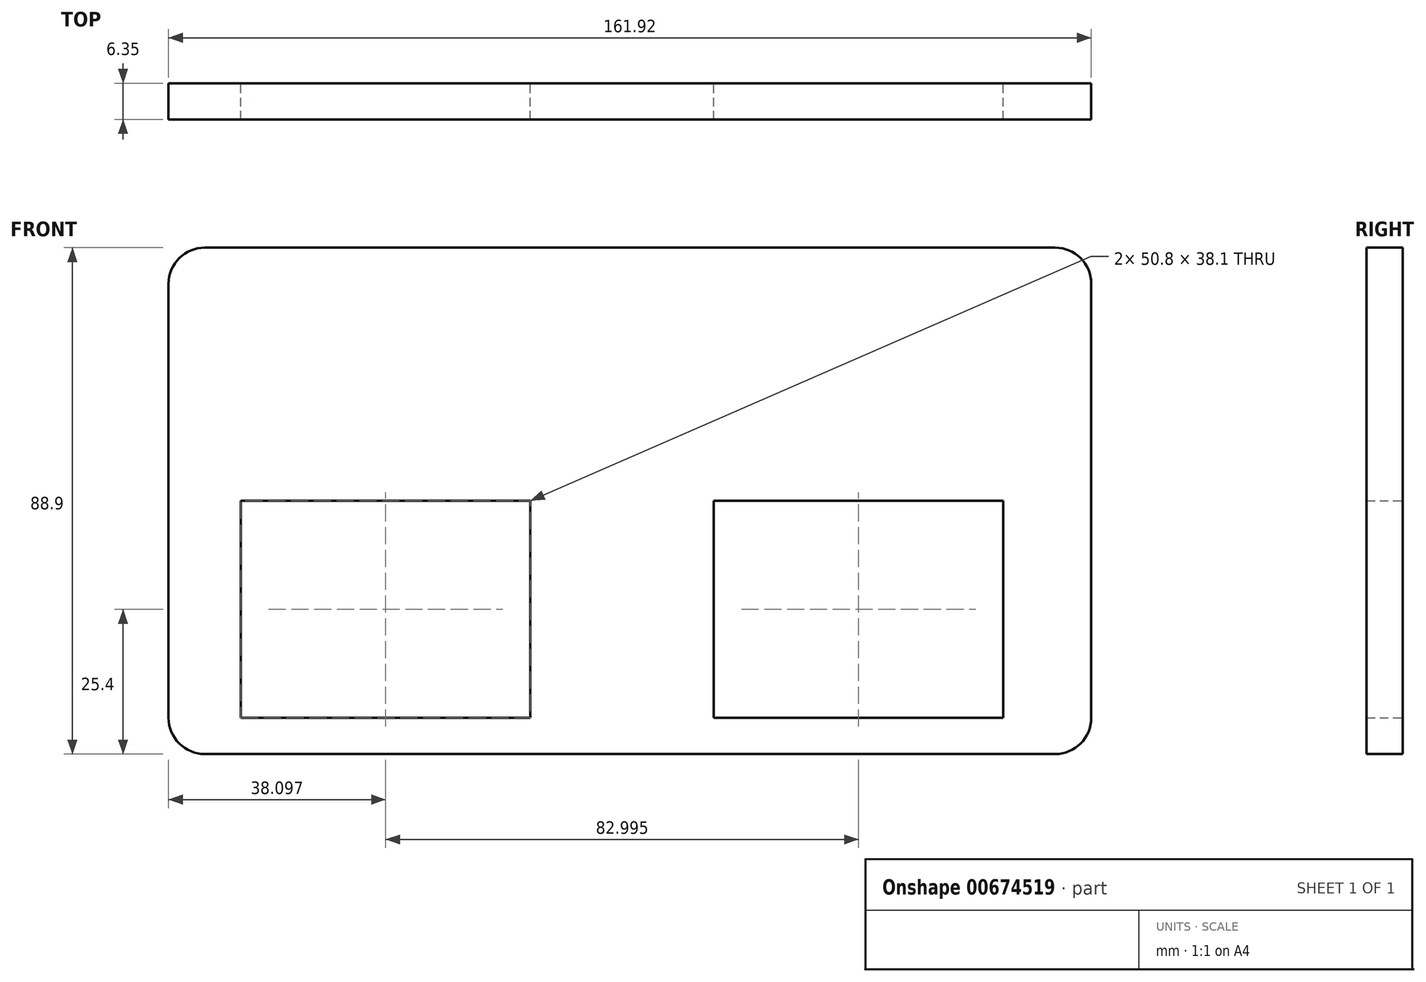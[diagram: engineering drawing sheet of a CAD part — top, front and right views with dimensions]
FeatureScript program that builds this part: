
annotation { "Feature Type Name" : "Feature", "Feature Type Description" : "" }
export const myFeature = defineFeature(function(context is Context, id is Id, definition is map)
    precondition{}
    {
        {
            var Q0;
            Q0=qCreatedBy(makeId("Front.planeOp"),FACE);
            var sketch = newSketch(context, id + "F0", { "sketchPlane" : qUnion([Q0])});
            skLineSegment(sketch, "E0.bottom", {"start": v(74.61, 44.45) * mm, "end": v(-74.61, 44.45) * mm});
            skLineSegment(sketch, "E0.top", {"start": v(74.61, -44.45) * mm, "end": v(-74.61, -44.45) * mm});
            skLineSegment(sketch, "E0.left", {"start": v(80.96, 38.1) * mm, "end": v(80.96, -38.1) * mm});
            skLineSegment(sketch, "E0.right", {"start": v(-80.96, 38.1) * mm, "end": v(-80.96, -38.1) * mm});
            skPoint(sketch, "E0.middle", {"position": v(0, 0) * mm});
            skPoint(sketch, "E1.visualSharp", {"position": v(80.96, 44.45) * mm});
            skArc(sketch, "E1.filletArc", {"start": v(80.96, 38.1) * mm, "mid": v(79.1, 42.6) * mm, "end": v(74.61, 44.45) * mm});
            skPoint(sketch, "E2.visualSharp", {"position": v(80.96, -44.45) * mm});
            skArc(sketch, "E2.filletArc", {"start": v(74.61, -44.45) * mm, "mid": v(79.1, -42.6) * mm, "end": v(80.96, -38.1) * mm});
            skPoint(sketch, "E3.visualSharp", {"position": v(-80.96, 44.45) * mm});
            skArc(sketch, "E3.filletArc", {"start": v(-74.61, 44.45) * mm, "mid": v(-79.1, 42.6) * mm, "end": v(-80.96, 38.1) * mm});
            skPoint(sketch, "E4.visualSharp", {"position": v(-80.96, -44.45) * mm});
            skArc(sketch, "E4.filletArc", {"start": v(-80.96, -38.1) * mm, "mid": v(-79.1, -42.6) * mm, "end": v(-74.61, -44.45) * mm});
            skLineSegment(sketch, "E5.bottom", {"start": v(-17.46, 0) * mm, "end": v(-68.26, 0) * mm});
            skLineSegment(sketch, "E5.top", {"start": v(-17.46, -38.1) * mm, "end": v(-68.26, -38.1) * mm});
            skLineSegment(sketch, "E5.left", {"start": v(-17.46, 0) * mm, "end": v(-17.46, -38.1) * mm});
            skLineSegment(sketch, "E5.right", {"start": v(-68.26, 0) * mm, "end": v(-68.26, -38.1) * mm});
            skPoint(sketch, "E5.middle", {"position": v(-42.86, -19.05) * mm});
            skLineSegment(sketch, "E6.bottom", {"start": v(65.53, 0) * mm, "end": v(14.73, 0) * mm});
            skLineSegment(sketch, "E6.top", {"start": v(65.53, -38.1) * mm, "end": v(14.73, -38.1) * mm});
            skLineSegment(sketch, "E6.left", {"start": v(65.53, 0) * mm, "end": v(65.53, -38.1) * mm});
            skLineSegment(sketch, "E6.right", {"start": v(14.73, 0) * mm, "end": v(14.73, -38.1) * mm});
            skPoint(sketch, "E6.middle", {"position": v(40.13, -19.05) * mm});
            skPoint(sketch, "E6.middle.positionSnap0", {"position": v(-17.46, -19.05) * mm});
            skPoint(sketch, "E6.centerSnap0", {"position": v(-17.46, -19.05) * mm});
            skSolve(sketch);
        }
        {
            var Q0;
            Q0 = qSketchRegion(id + "F0", true);
            extrude(context, id + "F1", {"entities" : qUnion([Q0]), "depth" : 6.35 * mm, "offsetDistance" : 25.4 * mm});
        }
    });
